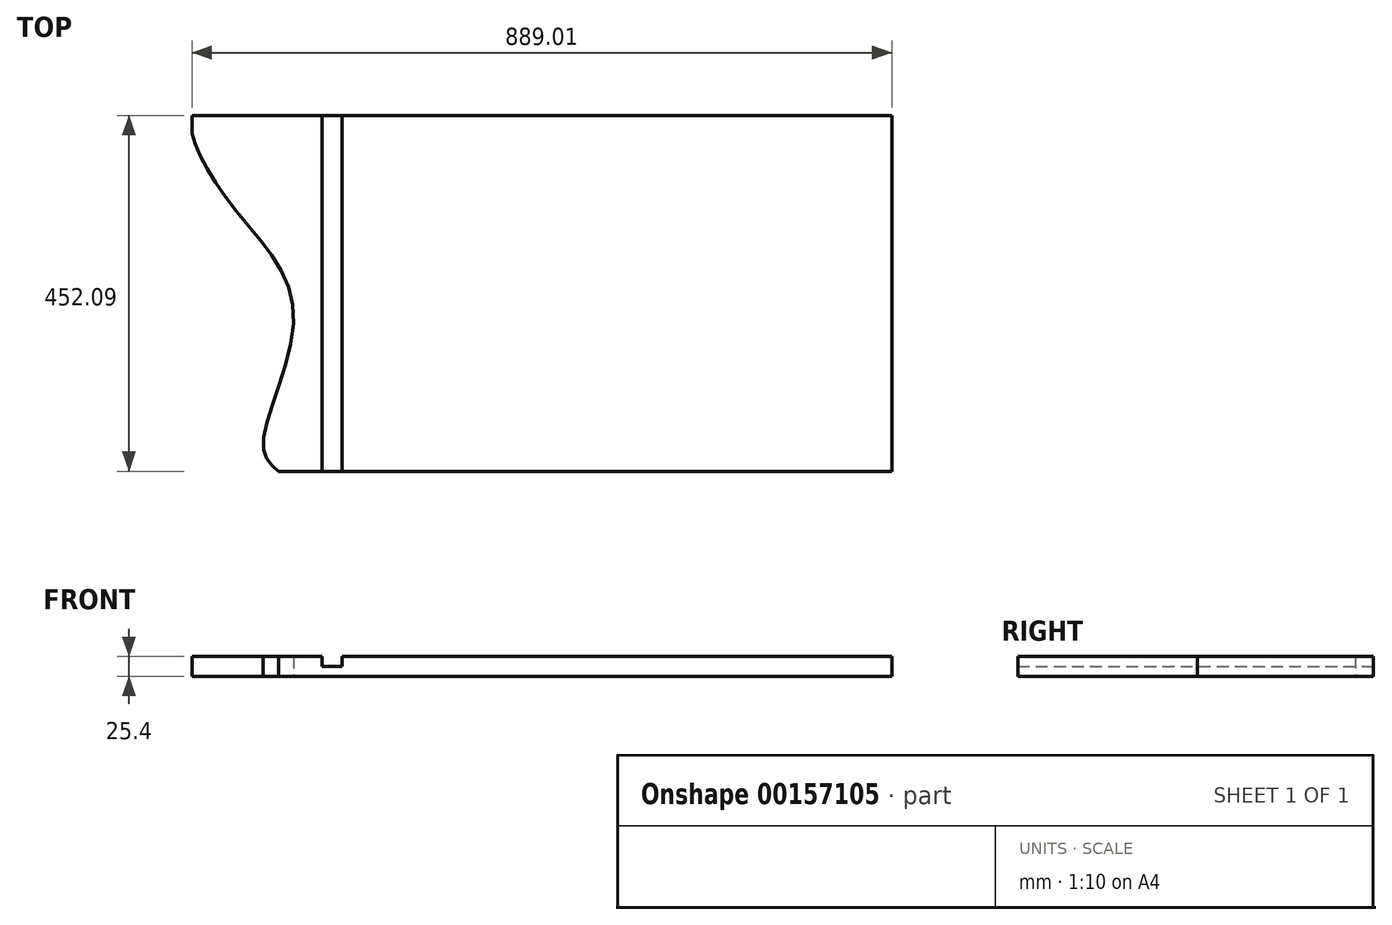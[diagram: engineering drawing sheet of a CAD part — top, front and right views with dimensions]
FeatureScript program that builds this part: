
annotation { "Feature Type Name" : "Feature", "Feature Type Description" : "" }
export const myFeature = defineFeature(function(context is Context, id is Id, definition is map)
    precondition{}
    {
        {
            var Q0;
            Q0=qCreatedBy(makeId("Top.planeOp"),FACE);
            var sketch = newSketch(context, id + "F0", { "sketchPlane" : qUnion([Q0])});
            skLineSegment(sketch, "E0.bottom", {"start": v(444.5, 114.3) * mm, "end": v(-444.5, 114.3) * mm});
            skLineSegment(sketch, "E0.top", {"start": v(444.5, -114.3) * mm, "end": v(-444.5, -114.3) * mm});
            skLineSegment(sketch, "E0.left", {"start": v(444.5, 114.3) * mm, "end": v(444.5, -114.3) * mm});
            skLineSegment(sketch, "E0.right", {"start": v(-444.5, 114.3) * mm, "end": v(-444.5, -114.3) * mm});
            skPoint(sketch, "E0.middle", {"position": v(0, 0) * mm});
            skLineSegment(sketch, "E1.bottom", {"start": v(444.5, -109.19) * mm, "end": v(-444.5, -109.19) * mm});
            skLineSegment(sketch, "E1.top", {"start": v(444.5, -337.79) * mm, "end": v(-444.5, -337.79) * mm});
            skLineSegment(sketch, "E1.left", {"start": v(444.5, -109.19) * mm, "end": v(444.5, -337.79) * mm});
            skLineSegment(sketch, "E1.right", {"start": v(-444.5, -109.19) * mm, "end": v(-444.5, -337.79) * mm});
            skPoint(sketch, "E1.middle", {"position": v(0, -223.49) * mm});
            skSolve(sketch);
        }
        {
            var Q0;
            Q0=qSketchRegion(id+"F0",true);
            extrude(context, id + "F1", {"entities" : qUnion([Q0]), "depth" : 25.4 * mm});
        }
        {
            var Q0;
            Q0=makeQuery(id+"F1.opExtrude","CAP_FACE",FACE,{"disambiguationData":[OSD([sQuery(id+"F0.wireOp",EDGE,"E0.bottom"),sQuery(id+"F0.wireOp",EDGE,"E0.top"),sQuery(id+"F0.wireOp",EDGE,"E0.left"),sQuery(id+"F0.wireOp",EDGE,"E0.right"),sQuery(id+"F0.wireOp",EDGE,"E1.bottom"),sQuery(id+"F0.wireOp",EDGE,"E1.top"),sQuery(id+"F0.wireOp",EDGE,"E1.left"),sQuery(id+"F0.wireOp",EDGE,"E1.right")])],"isStart":false});
            var sketch = newSketch(context, id + "F2", { "sketchPlane" : qUnion([Q0])});
            skLineSegment(sketch, "E2", {"start": v(-444.5, 114.3) * mm, "end": v(-266.7, 114.3) * mm});
            skLineSegment(sketch, "E3.bottom", {"start": v(-254, -387.72) * mm, "end": v(-279.4, -387.72) * mm});
            skLineSegment(sketch, "E3.top", {"start": v(-254, 616.32) * mm, "end": v(-279.4, 616.32) * mm});
            skLineSegment(sketch, "E3.left", {"start": v(-254, -387.72) * mm, "end": v(-254, 616.32) * mm});
            skLineSegment(sketch, "E3.right", {"start": v(-279.4, -387.72) * mm, "end": v(-279.4, 616.32) * mm});
            skPoint(sketch, "E3.middle", {"position": v(-266.7, 114.3) * mm});
            skSolve(sketch);
        }
        {
            var Q0;
            {var subQ0=sQuery(id+"F2.wireOp",EDGE,"E2");var subQ1=makeQuery(id+"F1.opExtrude","CAP_EDGE",EDGE,{"disambiguationData":[OSD([sQuery(id+"F0.wireOp",EDGE,"E0.bottom")])],"isStart":false});var subQ2=makeQuery(id+"F2.imprint","INTERSECT",VERTEX,{"derivedFrom":[subQ1,subQ0]});Q0=makeQuery(id+"F2.imprint","IMPRINT",FACE,{"disambiguationData":[TD([[makeQuery(id+"F2.imprint","IMPRINT",EDGE,{"disambiguationData":[TD([[subQ2,-1.0]])],"derivedFrom":subQ0}),1.0]])]});}
            extrude(context, id + "F3", {"entities" : qUnion([Q0]), "operationType" : NewBodyOperationType.REMOVE, "oppositeDirection" : true, "depth" : 12.7 * mm});
        }
        {
            var Q0;
            Q0=makeQuery(id+"F1.opExtrude","CAP_FACE",FACE,{"disambiguationData":[OSD([sQuery(id+"F0.wireOp",EDGE,"E0.bottom"),sQuery(id+"F0.wireOp",EDGE,"E0.top"),sQuery(id+"F0.wireOp",EDGE,"E0.left"),sQuery(id+"F0.wireOp",EDGE,"E0.right"),sQuery(id+"F0.wireOp",EDGE,"E1.bottom"),sQuery(id+"F0.wireOp",EDGE,"E1.top"),sQuery(id+"F0.wireOp",EDGE,"E1.left"),sQuery(id+"F0.wireOp",EDGE,"E1.right")])],"isStart":true});
            var sketch = newSketch(context, id + "F4", { "sketchPlane" : qUnion([Q0])});
            skPoint(sketch, "E4.2.internal.snap0", {"position": v(-444.5, 0) * mm});
            skFitSpline(sketch, "E4", {"points": [v(-444.5, -114.3) * mm, v(-444.5, -91.35) * mm, v(-393.81, 0) * mm, v(-315.35, 135.44) * mm, v(-353.94, 304.03) * mm, v(-334.25, 337.79) * mm], "startDerivative": vector(-31.92, 192.33) * mm, "endDerivative": vector(219.47, 187.26) * mm});
            skSolve(sketch);
        }
        {
            var Q0;
            {var subQ1=makeQuery(id+"F1.opExtrude","CAP_EDGE",EDGE,{"disambiguationData":[OSD([sQuery(id+"F0.wireOp",EDGE,"E0.top")])],"isStart":true});Q0=makeQuery(id+"F4.imprint","IMPRINT",FACE,{"disambiguationData":[TD([[makeQuery(id+"F4.imprint","IMPRINT",EDGE,{"derivedFrom":subQ1}),1.0]])]});}
            extrude(context, id + "F5", {"entities" : qUnion([Q0]), "operationType" : NewBodyOperationType.REMOVE, "oppositeDirection" : true, "depth" : 25.4 * mm});
        }
    });
